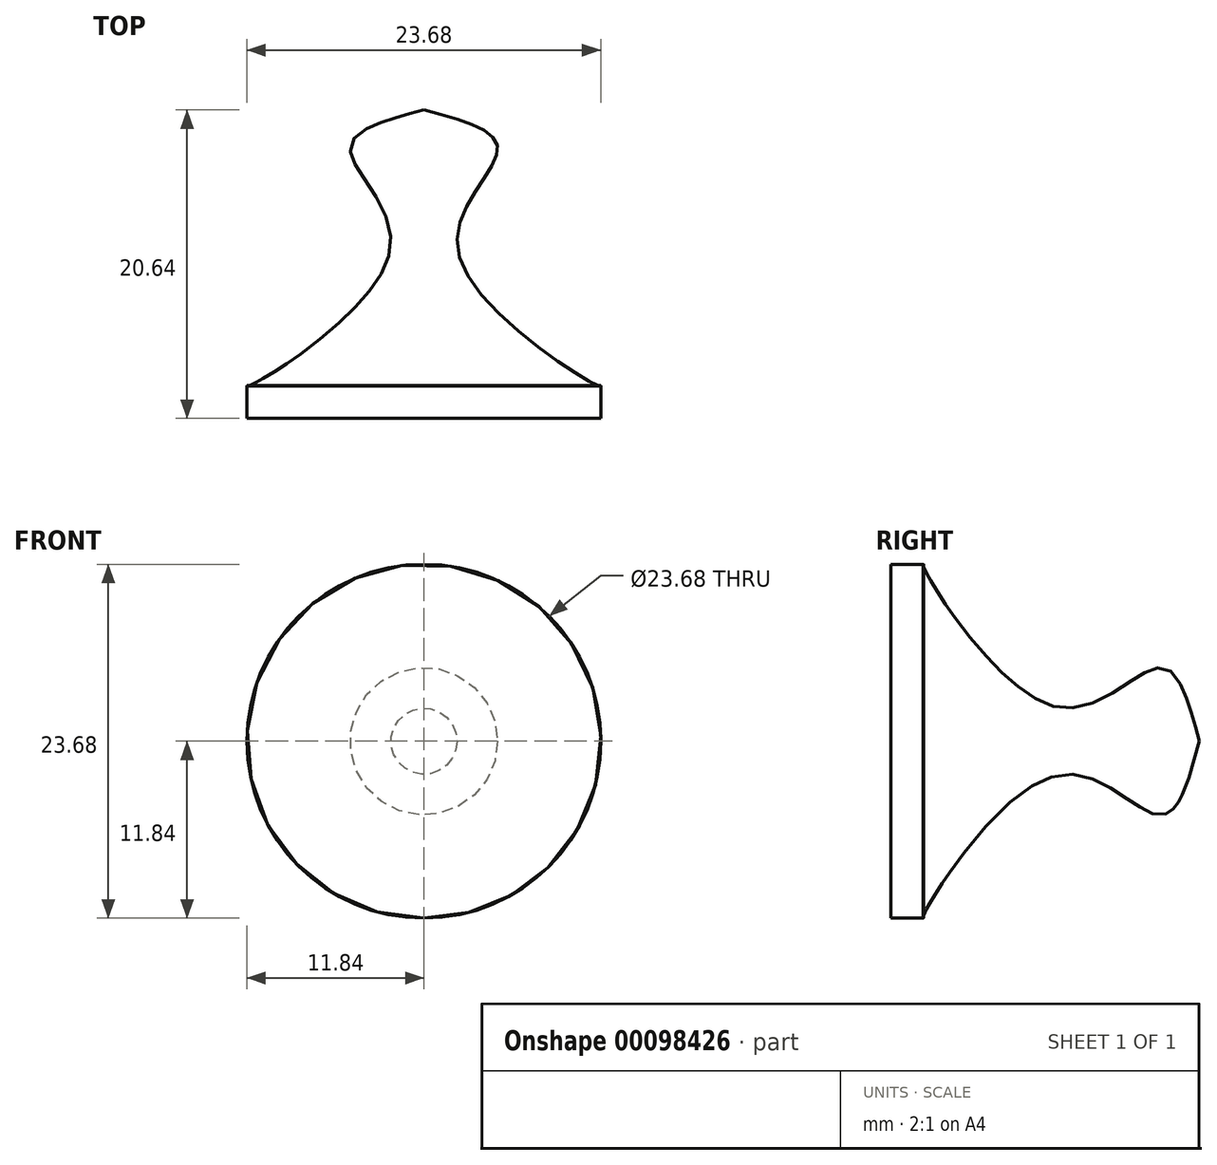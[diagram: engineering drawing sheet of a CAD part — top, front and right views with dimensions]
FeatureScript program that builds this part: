
annotation { "Feature Type Name" : "Feature", "Feature Type Description" : "" }
export const myFeature = defineFeature(function(context is Context, id is Id, definition is map)
    precondition{}
    {
        {
            var Q0;
            Q0=qCreatedBy(makeId("Top.planeOp"),FACE);
            var sketch = newSketch(context, id + "F0", { "sketchPlane" : qUnion([Q0])});
            skLineSegment(sketch, "E0", {"start": v(0, 0) * mm, "end": v(0, 20.64) * mm});
            skFitSpline(sketch, "E1", {"points": [v(0, 20.64) * mm, v(4.94, 18.02) * mm, v(2.32, 10.96) * mm, v(11.82, 2.16) * mm, v(11.82, 2.25) * mm], "startDerivative": vector(28.26, -7.33) * mm, "endDerivative": vector(-1.57, 3.68) * mm});
            skLineSegment(sketch, "E2", {"start": v(11.84, 2.2) * mm, "end": v(11.84, 0) * mm});
            skLineSegment(sketch, "E3", {"start": v(11.84, 0) * mm, "end": v(0, 0) * mm});
            skSolve(sketch);
        }
        {
            var Q0;
            Q0 = qSketchRegion(id + "F0", true);
            var Q1;
            Q1=sQuery(id+"F0.wireOp",EDGE,"E0");
            revolve(context, id + "F1", {"entities" : qUnion([Q0]), "axis" : qUnion([Q1]), "revolveType" : RevolveType.FULL});
        }
    });
